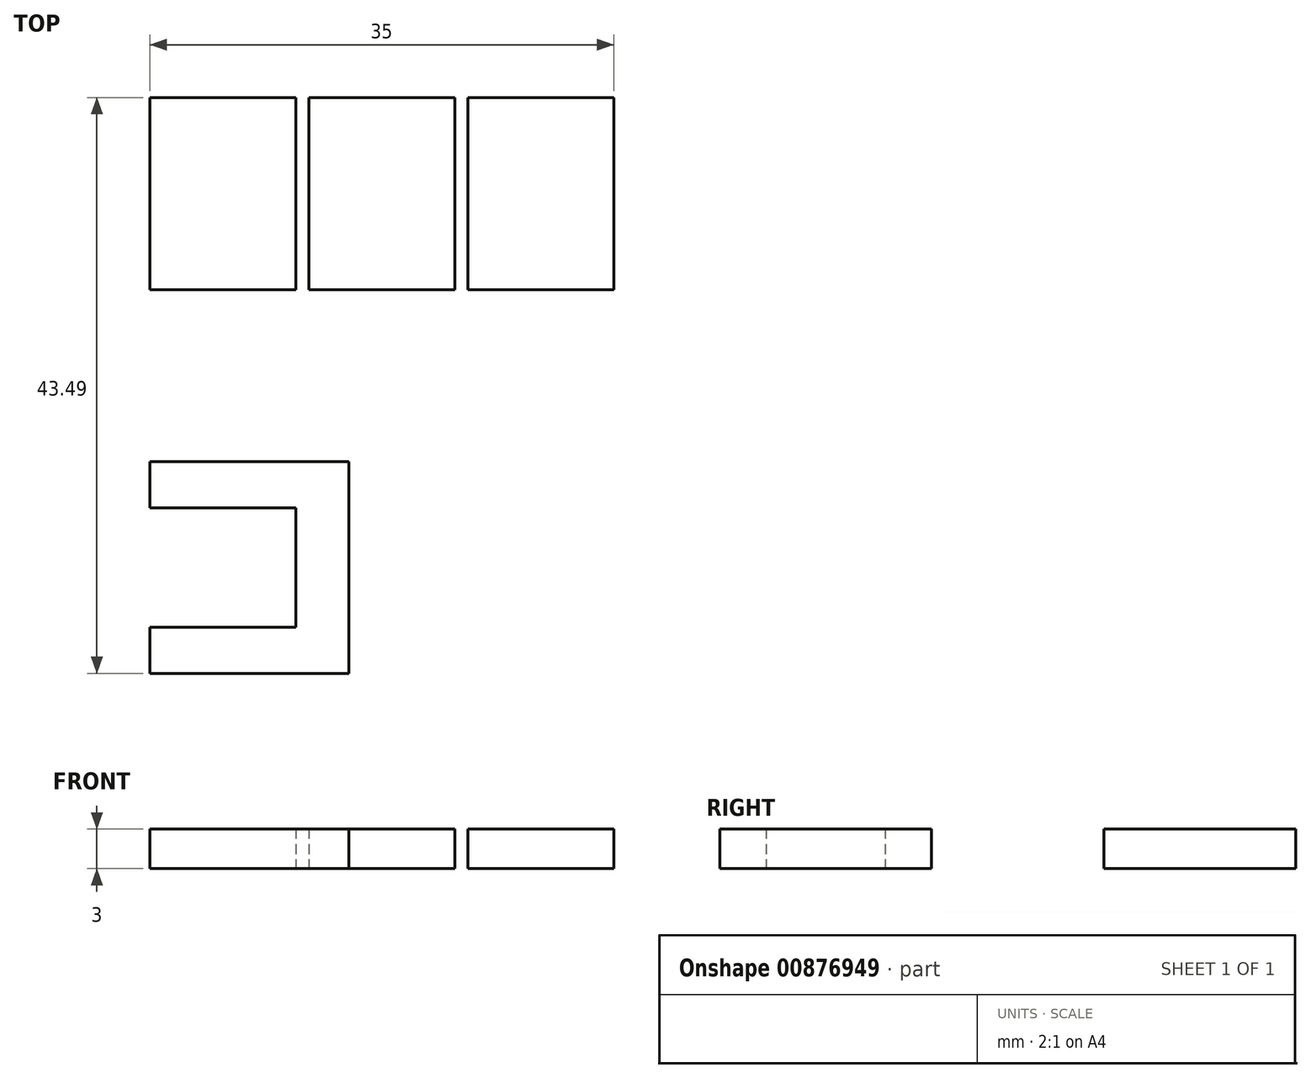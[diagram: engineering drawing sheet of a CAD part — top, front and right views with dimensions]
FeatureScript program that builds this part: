
annotation { "Feature Type Name" : "Feature", "Feature Type Description" : "" }
export const myFeature = defineFeature(function(context is Context, id is Id, definition is map)
    precondition{}
    {
        {
            var Q0;
            Q0=qCreatedBy(makeId("Top.planeOp"),FACE);
            var sketch = newSketch(context, id + "F0", { "sketchPlane" : qUnion([Q0])});
            skLineSegment(sketch, "E0.bottom", {"start": v(0, 0) * mm, "end": v(11, 0) * mm});
            skLineSegment(sketch, "E0.top", {"start": v(0, 14.5) * mm, "end": v(11, 14.5) * mm});
            skLineSegment(sketch, "E0.left", {"start": v(0, 0) * mm, "end": v(0, 14.5) * mm});
            skLineSegment(sketch, "E0.right", {"start": v(11, 0) * mm, "end": v(11, 14.5) * mm});
            skLineSegment(sketch, "E1.1.0.0", {"start": v(12, 0) * mm, "end": v(12, 14.5) * mm});
            skLineSegment(sketch, "E1.1.0.1", {"start": v(12, 14.5) * mm, "end": v(23, 14.5) * mm});
            skLineSegment(sketch, "E1.1.0.2", {"start": v(23, 0) * mm, "end": v(23, 14.5) * mm});
            skLineSegment(sketch, "E1.1.0.3", {"start": v(12, 0) * mm, "end": v(23, 0) * mm});
            skLineSegment(sketch, "E1.2.0.0", {"start": v(24, 0) * mm, "end": v(24, 14.5) * mm});
            skLineSegment(sketch, "E1.2.0.1", {"start": v(24, 14.5) * mm, "end": v(35, 14.5) * mm});
            skLineSegment(sketch, "E1.2.0.2", {"start": v(35, 0) * mm, "end": v(35, 14.5) * mm});
            skLineSegment(sketch, "E1.2.0.3", {"start": v(24, 0) * mm, "end": v(35, 0) * mm});
            skLineSegment(sketch, "E1.direction1", {"start": v(0, 0) * mm, "end": v(12, 0) * mm, "construction": true});
            skLineSegment(sketch, "E2", {"start": v(0, -13) * mm, "end": v(15, -13) * mm});
            skLineSegment(sketch, "E3", {"start": v(15, -13) * mm, "end": v(15, -29) * mm});
            skLineSegment(sketch, "E4", {"start": v(15, -29) * mm, "end": v(0, -29) * mm});
            skLineSegment(sketch, "E5", {"start": v(0, -29) * mm, "end": v(0, -25.5) * mm});
            skLineSegment(sketch, "E6", {"start": v(0, -25.5) * mm, "end": v(11, -25.5) * mm});
            skLineSegment(sketch, "E7", {"start": v(11, -25.5) * mm, "end": v(11, -16.5) * mm});
            skLineSegment(sketch, "E8", {"start": v(11, -16.5) * mm, "end": v(0, -16.5) * mm});
            skLineSegment(sketch, "E9", {"start": v(0, -16.5) * mm, "end": v(0, -13) * mm});
            skPoint(sketch, "E10", {"position": v(11, -21) * mm});
            skPoint(sketch, "E11", {"position": v(15, -21) * mm});
            skSolve(sketch);
        }
        {
            var Q0;
            Q0 = qSketchRegion(id + "F0", true);
            extrude(context, id + "F1", {"entities" : qUnion([Q0]), "depth" : 3 * mm, "offsetDistance" : 25 * mm});
        }
    });
